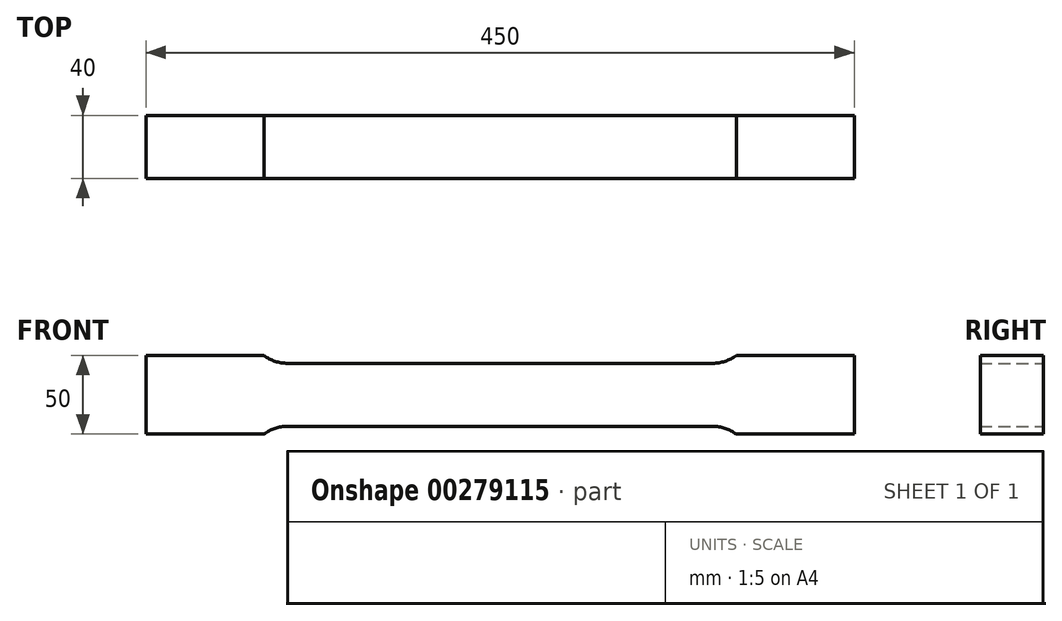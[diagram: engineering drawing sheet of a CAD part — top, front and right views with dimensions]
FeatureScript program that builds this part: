
annotation { "Feature Type Name" : "Feature", "Feature Type Description" : "" }
export const myFeature = defineFeature(function(context is Context, id is Id, definition is map)
    precondition{}
    {
        {
            var Q0;
            Q0=qCreatedBy(makeId("Front.planeOp"),FACE);
            var sketch = newSketch(context, id + "F0", { "sketchPlane" : qUnion([Q0])});
            skLineSegment(sketch, "E0", {"start": v(0, 20) * mm, "end": v(135, 20) * mm});
            skArc(sketch, "E1", {"start": v(135, 20) * mm, "mid": v(142.9, 21.28) * mm, "end": v(150, 25) * mm});
            skLineSegment(sketch, "E2", {"start": v(150, 25) * mm, "end": v(225, 25) * mm});
            skLineSegment(sketch, "E3", {"start": v(225, 25) * mm, "end": v(225, 0) * mm});
            skLineSegment(sketch, "E4.MirrorCS", {"start": v(0, -20) * mm, "end": v(135, -20) * mm});
            skLineSegment(sketch, "E5.MirrorCS", {"start": v(225, -25) * mm, "end": v(225, 0) * mm});
            skLineSegment(sketch, "E6.MirrorCS", {"start": v(150, -25) * mm, "end": v(225, -25) * mm});
            skArc(sketch, "E7.MirrorCS", {"start": v(135, -20) * mm, "mid": v(142.9, -21.28) * mm, "end": v(150, -25) * mm});
            skArc(sketch, "E8.MirrorCS", {"start": v(-135, -20) * mm, "mid": v(-142.9, -21.28) * mm, "end": v(-150, -25) * mm});
            skLineSegment(sketch, "E9.MirrorCS", {"start": v(-150, -25) * mm, "end": v(-225, -25) * mm});
            skArc(sketch, "E10.MirrorCS", {"start": v(-135, 20) * mm, "mid": v(-142.9, 21.28) * mm, "end": v(-150, 25) * mm});
            skLineSegment(sketch, "E11.MirrorCS", {"start": v(-150, 25) * mm, "end": v(-225, 25) * mm});
            skLineSegment(sketch, "E12.MirrorCS", {"start": v(-225, -25) * mm, "end": v(-225, 0) * mm});
            skLineSegment(sketch, "E13.MirrorCS", {"start": v(0, -20) * mm, "end": v(-135, -20) * mm});
            skLineSegment(sketch, "E14.MirrorCS", {"start": v(-225, 25) * mm, "end": v(-225, 0) * mm});
            skLineSegment(sketch, "E15.MirrorCS", {"start": v(0, 20) * mm, "end": v(-135, 20) * mm});
            skSolve(sketch);
        }
        {
            var Q0;
            Q0 = qSketchRegion(id + "F0", true);
            extrude(context, id + "F1", {"entities" : qUnion([Q0]), "endBound" : BoundingType.SYMMETRIC, "depth" : 40 * mm});
        }
        {
            var Q0;
            Q0 = qSketchRegion(id + "F0", true);
            extrude(context, id + "F2", {"entities" : qUnion([Q0]), "operationType" : NewBodyOperationType.ADD, "endBound" : BoundingType.SYMMETRIC, "depth" : 12.5 * mm});
        }
    });
